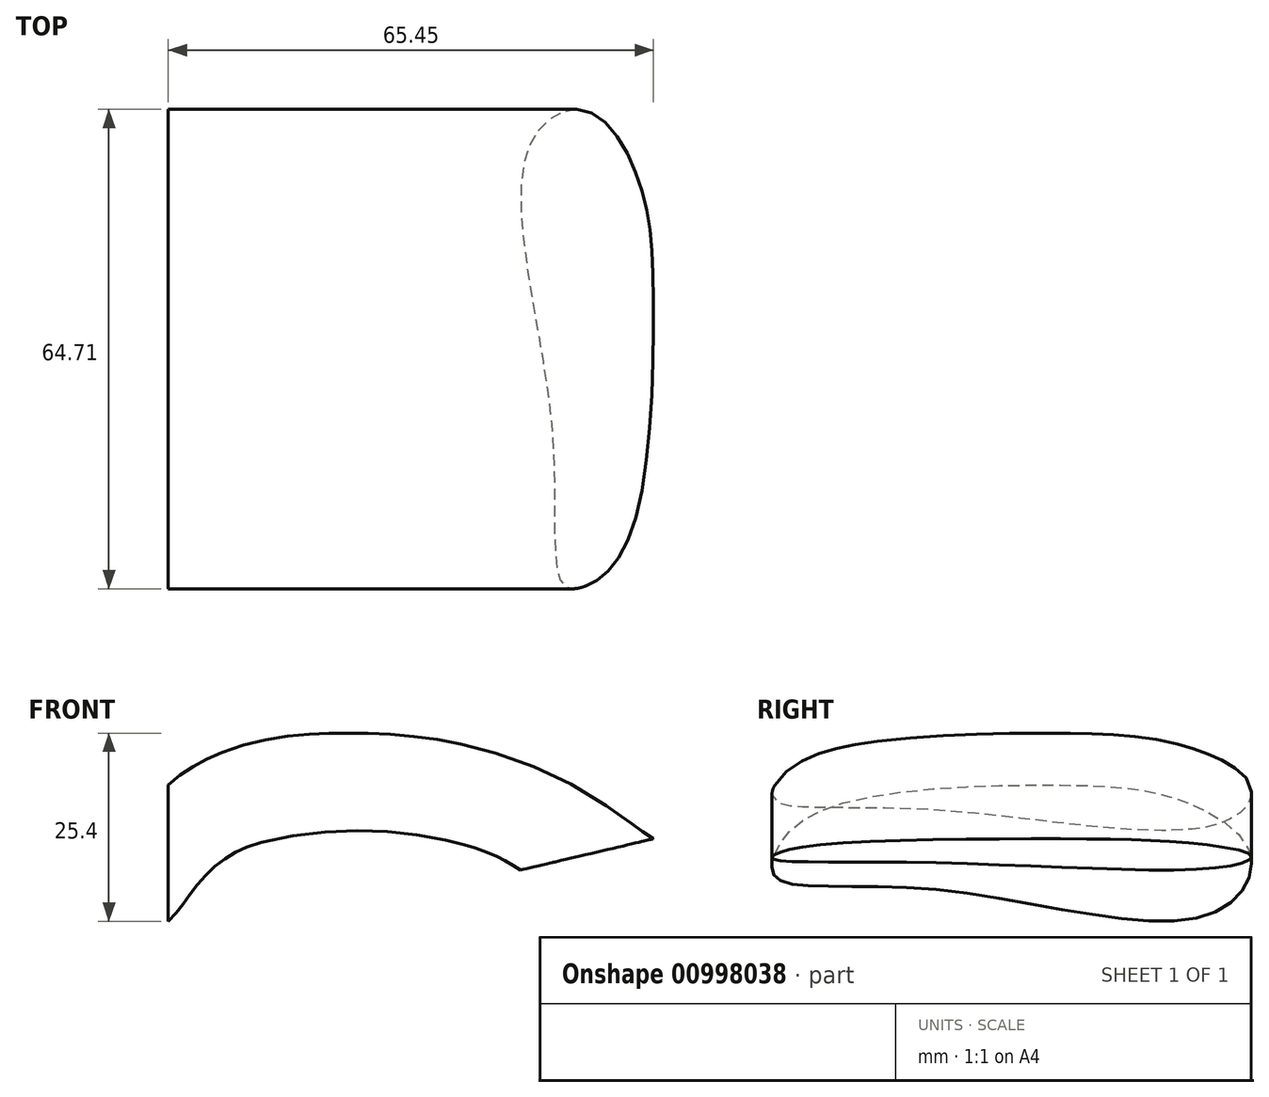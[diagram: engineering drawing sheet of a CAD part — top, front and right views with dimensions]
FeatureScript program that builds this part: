
annotation { "Feature Type Name" : "Feature", "Feature Type Description" : "" }
export const myFeature = defineFeature(function(context is Context, id is Id, definition is map)
    precondition{}
    {
        {
            var Q0;
            Q0=qCreatedBy(makeId("Right.planeOp"),FACE);
            var sketch = newSketch(context, id + "F0", { "sketchPlane" : qUnion([Q0])});
            skFitSpline(sketch, "E0", {"points": [v(-26.55, 0) * mm, v(-19.85, 6.13) * mm, v(12.34, 9.4) * mm, v(28.51, 7.27) * mm, v(37.66, 0) * mm, v(32.1, -8.09) * mm, v(-5.15, -4.66) * mm, v(-26.22, -3.19) * mm, v(-26.55, 0) * mm]});
            skSolve(sketch);
        }
        {
            var Q0;
            Q0=qCreatedBy(makeId("Front.planeOp"),FACE);
            var sketch = newSketch(context, id + "F1", { "sketchPlane" : qUnion([Q0])});
            skFitSpline(sketch, "E1", {"points": [v(0, 0) * mm, v(4.17, 3.68) * mm, v(12.99, 7.92) * mm, v(32.76, 8.9) * mm, v(48.12, 4.66) * mm, v(56.29, 0) * mm], "startDerivative": vector(27.42, 26.58) * mm, "endDerivative": vector(41.6, -26.64) * mm});
            skSolve(sketch);
        }
        {
            var Q0;
            Q0=makeQuery(id+"F0.imprint","IMPRINT",FACE,{"disambiguationData":[TD([[makeQuery(id+"F0.imprint","IMPRINT",EDGE,{"derivedFrom":sQuery(id+"F0.wireOp",EDGE,"E0")}),-1.0]])]});
            var Q1;
            Q1=sQuery(id+"F0.wireOp",EDGE,"E0");
            var Q2;
            Q2=sQuery(id+"F1.wireOp",EDGE,"E1");
            sweep(context, id + "F2", {"profiles" : qUnion([Q0]), "surfaceProfiles" : qUnion([Q1]), "path" : qUnion([Q2])});
        }
    });
